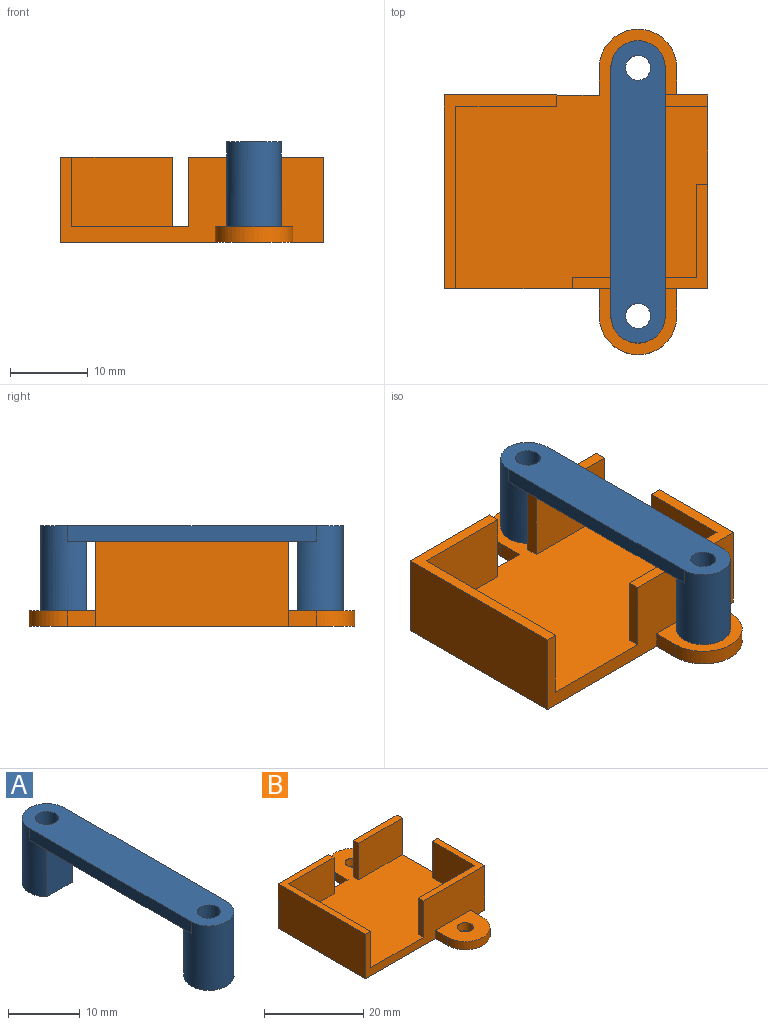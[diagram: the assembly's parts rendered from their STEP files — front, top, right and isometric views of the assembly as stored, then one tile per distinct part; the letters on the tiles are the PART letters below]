
ASSEMBLY  parts=2 mates=1
PART A: 12 faces, bbox 7x39x11 mm
  f0: cylinder r=3.5mm len=11mm, axis (0,0,-1), area 169.8mm2, adj f4,f5,f6,f7,f8,f11
  f1: cylinder r=3.5mm len=11mm, axis (0,0,-1), area 169.8mm2, adj f3,f4,f5,f6,f7,f10
  f2: cylinder r=1.6mm len=11mm, axis (0,0,-1), area 110.6mm2, adj f3,f7
  f3: plane 7x5.95mm, normal (0,0,-1), area 26.8mm2, adj f1,f2,f10
  f4: plane 32x7mm, normal (0,0,-1), area 192.8mm2, adj f0,f1,f5,f6,f10,f11
  f5: plane 32x2mm, normal (1,0,0), area 64mm2, adj f0,f1,f4,f7
  f6: plane 32x2mm, normal (-1,0,0), area 64mm2, adj f0,f1,f4,f7
  f7: plane 39x7mm, normal (0,0,1), area 246.4mm2, adj f0,f1,f2,f5,f6,f9
  f8: plane 7x5.95mm, normal (0,0,-1), area 26.8mm2, adj f0,f9,f11
  f9: cylinder r=1.6mm len=11mm, axis (0,0,-1), area 110.6mm2, adj f7,f8
  f10: plane 9x5mm, normal (0,-1,0), area 45mm2, adj f1,f3,f4
  f11: plane 9x5mm, normal (0,1,0), area 45mm2, adj f0,f4,f8
PART B: 28 faces, bbox 34x42x11 mm
  f0: plane 20x11mm, normal (0,1,0), area 170.5mm2, adj f6,f10,f11,f14,f18,f23
  f1: plane 34x11mm, normal (0,-1,0), area 219mm2, adj f5,f6,f9,f10,f11,f12,f14,f16
  f2: plane 16x9mm, normal (0,1,0), area 144mm2, adj f3,f5,f14,f16
  f3: plane 12x9mm, normal (-1,0,0), area 108mm2, adj f2,f5,f14,f15
  f4: plane 12.5x1.5mm, normal (0,0,1), area 18.8mm2, adj f7,f8,f9,f17
  f5: plane 17.5x13.5mm, normal (0,0,1), area 44.3mm2, adj f1,f2,f3,f9,f15,f16
  f6: plane 25x14.5mm, normal (0,0,1), area 57mm2, adj f0,f1,f10,f12,f13,f18
  f7: plane 12.5x9mm, normal (0,-1,0), area 112.5mm2, adj f4,f9,f14,f17
  f8: plane 12.5x11mm, normal (0,1,0), area 120.5mm2, adj f4,f9,f11,f14,f17,f24
  f9: plane 25x11mm, normal (1,0,0), area 185mm2, adj f1,f4,f5,f7,f8,f11,f14,f15
  f10: plane 25x11mm, normal (-1,0,0), area 275mm2, adj f0,f1,f6,f11
  f11: plane 42x34mm, normal (0,0,-1), area 982.5mm2, adj f0,f1,f8,f9,f10,f19,f21,f22
  f12: plane 23.5x9mm, normal (1,0,0), area 211.5mm2, adj f1,f6,f13,f14
  f13: plane 13x9mm, normal (0,-1,0), area 117mm2, adj f6,f12,f14,f18
  f14: plane 33.5x32.5mm, normal (0,0,1), area 796.2mm2, adj f0,f1,f2,f3,f7,f8,f9,f12
  f15: plane 9x1.5mm, normal (0,1,0), area 13.5mm2, adj f3,f5,f9,f14
  f16: plane 9x1.5mm, normal (-1,0,0), area 13.5mm2, adj f1,f2,f5,f14
  f17: plane 9x1.5mm, normal (-1,0,0), area 13.5mm2, adj f4,f7,f8,f14
  f18: plane 9x1.5mm, normal (1,0,0), area 13.5mm2, adj f0,f6,f13,f14
  f19: cylinder r=5mm len=10mm, axis (0,0,-1), area 31.4mm2, adj f11,f20,f21,f22
  f20: plane 10x8.5mm, normal (0,0,1), area 66.2mm2, adj f1,f19,f21,f22,f26
  f21: plane 3.5x2mm, normal (1,0,0), area 7mm2, adj f1,f11,f19,f20
  f22: plane 3.5x2mm, normal (-1,0,0), area 7mm2, adj f1,f11,f19,f20
  f23: plane 3.5x2mm, normal (-1,0,0), area 7mm2, adj f0,f11,f14,f25
  f24: plane 3.5x2mm, normal (1,0,0), area 7mm2, adj f8,f11,f14,f25
  f25: cylinder r=5mm len=10mm, axis (0,0,-1), area 31.4mm2, adj f11,f14,f23,f24
  f26: cylinder r=1.6mm len=3.2mm, axis (0,0,1), area 20.1mm2, adj f11,f20
  f27: cylinder r=1.6mm len=3.2mm, axis (0,0,1), area 20.1mm2, adj f11,f14
PLACE A t=(65.12,-76.76,-0.65)mm
PLACE B t=(2.14,-31.23,-2.65)mm
MATE fastened A.f1 <-> B.f25  axis (0,0,-1) through (40.58,-40.56,-0.65)mm
